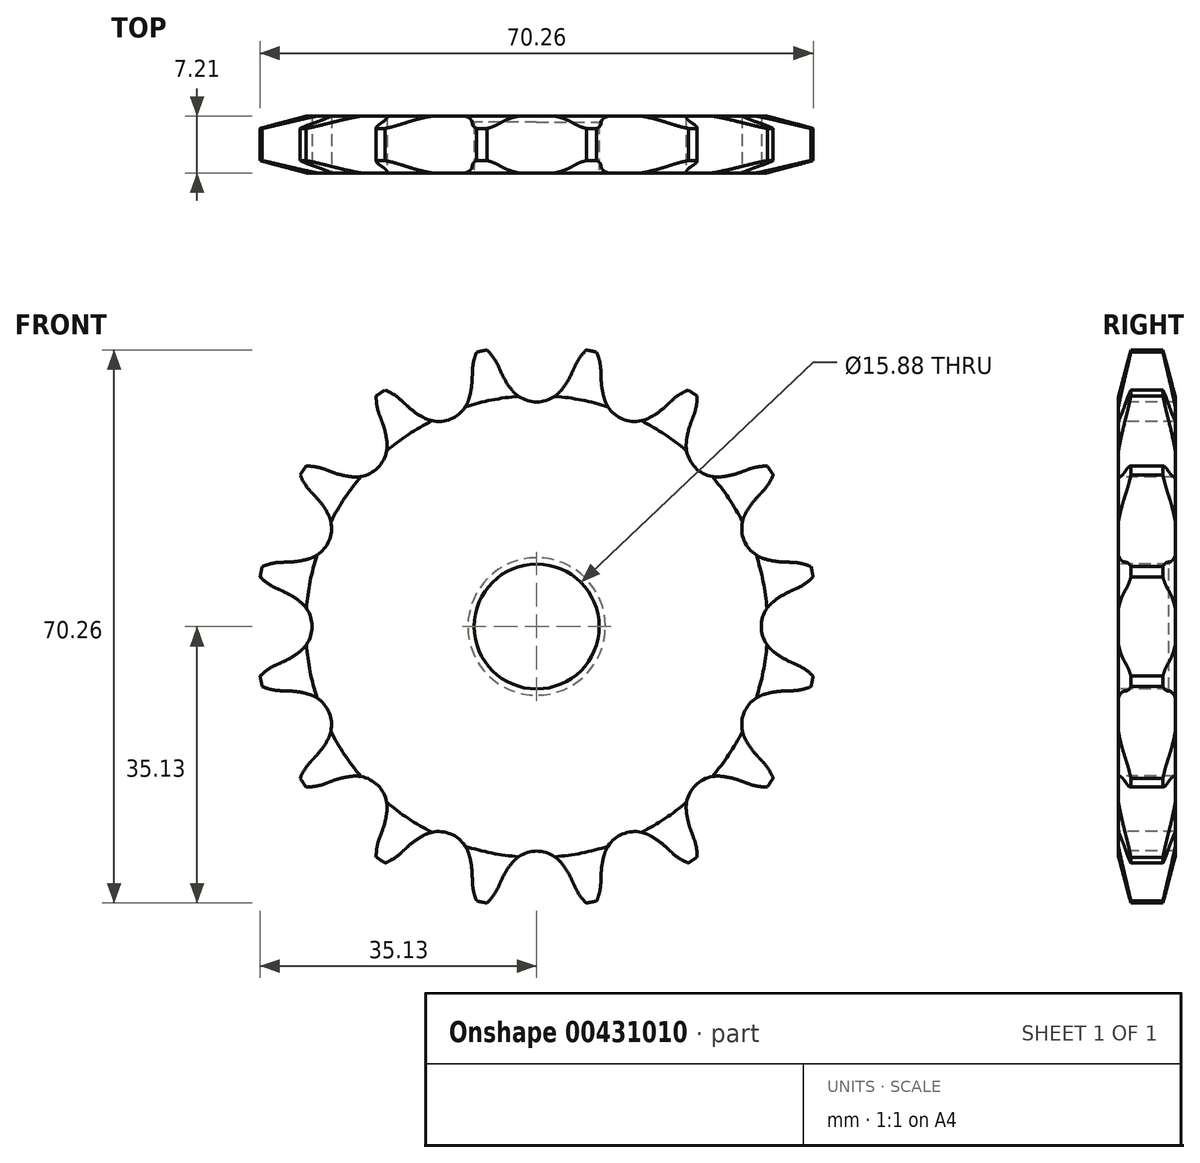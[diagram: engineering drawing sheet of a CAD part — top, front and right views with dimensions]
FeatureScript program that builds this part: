
annotation { "Feature Type Name" : "Feature", "Feature Type Description" : "" }
export const myFeature = defineFeature(function(context is Context, id is Id, definition is map)
    precondition{}
    {
        {
            var Q0;
            Q0=qCreatedBy(makeId("Right.planeOp"),FACE);
            var sketch = newSketch(context, id + "F0", { "sketchPlane" : qUnion([Q0])});
            skLineSegment(sketch, "E0", {"start": v(0, 0) * mm, "end": v(7.21, 0) * mm, "construction": true});
            skLineSegment(sketch, "E1", {"start": v(0, 35.69) * mm, "end": v(7.21, 35.69) * mm});
            skLineSegment(sketch, "E2", {"start": v(7.21, 35.69) * mm, "end": v(7.21, 25.4) * mm});
            skLineSegment(sketch, "E3", {"start": v(7.21, 25.4) * mm, "end": v(7.21, 25.4) * mm});
            skLineSegment(sketch, "E4", {"start": v(7.21, 25.4) * mm, "end": v(7.21, 7.94) * mm});
            skLineSegment(sketch, "E5", {"start": v(7.21, 7.94) * mm, "end": v(0, 7.94) * mm});
            skLineSegment(sketch, "E6", {"start": v(0, 7.94) * mm, "end": v(0, 35.69) * mm});
            skLineSegment(sketch, "E7.0.MirrorCS", {"start": v(0, -35.69) * mm, "end": v(7.21, -35.69) * mm});
            skLineSegment(sketch, "E7.1.MirrorCS", {"start": v(7.21, -35.69) * mm, "end": v(7.21, -25.4) * mm});
            skLineSegment(sketch, "E7.2.MirrorCS", {"start": v(7.21, -7.94) * mm, "end": v(0, -7.94) * mm});
            skLineSegment(sketch, "E7.3.MirrorCS", {"start": v(7.21, -25.4) * mm, "end": v(7.21, -7.94) * mm});
            skLineSegment(sketch, "E7.4.MirrorCS", {"start": v(7.21, -25.4) * mm, "end": v(7.21, -25.4) * mm});
            skLineSegment(sketch, "E7.5.MirrorCS", {"start": v(0, -7.94) * mm, "end": v(0, -35.69) * mm});
            skSolve(sketch);
        }
        {
            var Q0;
            Q0=makeQuery(id+"F0.imprint","IMPRINT",FACE,{"disambiguationData":[TD([[makeQuery(id+"F0.imprint","IMPRINT",EDGE,{"derivedFrom":sQuery(id+"F0.wireOp",EDGE,"E1")}),-1.0]])]});
            var Q1;
            Q1=sQuery(id+"F0.wireOp",EDGE,"E0");
            revolve(context, id + "F1", {"entities" : qUnion([Q0]), "axis" : qUnion([Q1]), "revolveType" : RevolveType.FULL});
        }
        {
            var Q0;
            Q0=makeQuery(id+"F1.opRevolve","SWEPT_EDGE",EDGE,{"disambiguationData":[OSD([sQuery(id+"F0.wireOp",EDGE,"E1"),sQuery(id+"F0.wireOp",EDGE,"E6")])]});
            var Q1;
            Q1=makeQuery(id+"F1.opRevolve","SWEPT_EDGE",EDGE,{"disambiguationData":[OSD([sQuery(id+"F0.wireOp",EDGE,"E1"),sQuery(id+"F0.wireOp",EDGE,"E2")])]});
            chamfer(context, id + "F2", {"entities" : qUnion([Q0, Q1]), "chamferType" : ChamferType.TWO_OFFSETS, "width1" : 6.35 * mm, "oppositeDirection" : false, "width2" : 1.57 * mm, "tangentPropagation" : true});
        }
        {
            var Q0;
            Q0=makeQuery(id+"F1.opRevolve","SWEPT_FACE",FACE,{"disambiguationData":[OSD([sQuery(id+"F0.wireOp",EDGE,"E6")])]});
            var sketch = newSketch(context, id + "F3", { "sketchPlane" : qUnion([Q0])});
            skCircle(sketch, "E8", {"center": v(0, 0) * mm, "radius": 32.55 * mm, "construction": true});
            skLineSegment(sketch, "E9", {"start": v(0, 0) * mm, "end": v(0, 32.55) * mm, "construction": true});
            skLineSegment(sketch, "E10", {"start": v(0, 32.55) * mm, "end": v(25.8, 32.55) * mm, "construction": true});
            skPoint(sketch, "E11", {"position": v(-10.88, 30.38) * mm});
            skPoint(sketch, "E12", {"position": v(4.95, 36.52) * mm});
            skLineSegment(sketch, "E13", {"start": v(0, 32.55) * mm, "end": v(4.95, 36.52) * mm, "construction": true});
            skLineSegment(sketch, "E14", {"start": v(4.95, 36.52) * mm, "end": v(-4.5, 32.26) * mm, "construction": true});
            skLineSegment(sketch, "E15", {"start": v(-4.5, 32.26) * mm, "end": v(-4.88, 33.1) * mm});
            skLineSegment(sketch, "E16", {"start": v(0, 0) * mm, "end": v(-7.12, 35.8) * mm, "construction": true});
            skArc(sketch, "E17", {"start": v(-7.12, 35.8) * mm, "mid": v(-15.95, 26.17) * mm, "end": v(-4.88, 33.1) * mm, "construction": true});
            skArc(sketch, "E18", {"start": v(-4.88, 33.1) * mm, "mid": v(-5.81, 34.6) * mm, "end": v(-7.12, 35.8) * mm});
            skArc(sketch, "E19", {"start": v(-3.14, 30.03) * mm, "mid": v(13.78, 41.93) * mm, "end": v(-4.5, 32.26) * mm, "construction": true});
            skArc(sketch, "E20", {"start": v(-4.5, 32.26) * mm, "mid": v(-3.89, 31.1) * mm, "end": v(-3.14, 30.03) * mm});
            skLineSegment(sketch, "E21", {"start": v(4.4, 12.5) * mm, "end": v(-4.88, 33.1) * mm, "construction": true});
            skArc(sketch, "E22.0.MirrorCS", {"start": v(4.5, 32.26) * mm, "mid": v(3.89, 31.1) * mm, "end": v(3.14, 30.03) * mm});
            skLineSegment(sketch, "E23.0.MirrorCS", {"start": v(4.5, 32.26) * mm, "end": v(4.88, 33.1) * mm});
            skArc(sketch, "E24.0.MirrorCS", {"start": v(4.88, 33.1) * mm, "mid": v(5.81, 34.6) * mm, "end": v(7.12, 35.8) * mm});
            skArc(sketch, "E25", {"start": v(-3.14, 30.03) * mm, "mid": v(0, 28.53) * mm, "end": v(3.14, 30.03) * mm});
            skArc(sketch, "E26", {"start": v(3.14, 30.03) * mm, "mid": v(0, 36.57) * mm, "end": v(-3.14, 30.03) * mm, "construction": true});
            skArc(sketch, "E27.1.0", {"start": v(-17.17, 28.7) * mm, "mid": v(-18.61, 29.74) * mm, "end": v(-20.28, 30.34) * mm});
            skLineSegment(sketch, "E27.1.1", {"start": v(-16.5, 28.08) * mm, "end": v(-17.17, 28.7) * mm});
            skArc(sketch, "E27.1.2", {"start": v(-16.5, 28.08) * mm, "mid": v(-15.5, 27.25) * mm, "end": v(-14.39, 26.55) * mm});
            skArc(sketch, "E27.1.3", {"start": v(-14.39, 26.55) * mm, "mid": v(-10.92, 26.36) * mm, "end": v(-8.6, 28.95) * mm});
            skArc(sketch, "E27.1.4", {"start": v(-8.19, 31.53) * mm, "mid": v(-8.3, 30.22) * mm, "end": v(-8.6, 28.95) * mm});
            skLineSegment(sketch, "E27.1.5", {"start": v(-8.19, 31.53) * mm, "end": v(-8.16, 32.44) * mm});
            skArc(sketch, "E27.1.6", {"start": v(-8.16, 32.44) * mm, "mid": v(-7.87, 34.19) * mm, "end": v(-7.12, 35.8) * mm});
            skArc(sketch, "E27.2.0", {"start": v(-26.85, 19.95) * mm, "mid": v(-28.57, 20.35) * mm, "end": v(-30.34, 20.28) * mm});
            skLineSegment(sketch, "E27.2.1", {"start": v(-26, 19.63) * mm, "end": v(-26.85, 19.95) * mm});
            skArc(sketch, "E27.2.2", {"start": v(-26, 19.63) * mm, "mid": v(-24.74, 19.24) * mm, "end": v(-23.45, 19.02) * mm});
            skArc(sketch, "E27.2.3", {"start": v(-23.45, 19.02) * mm, "mid": v(-20.17, 20.17) * mm, "end": v(-19.02, 23.45) * mm});
            skArc(sketch, "E27.2.4", {"start": v(-19.63, 26) * mm, "mid": v(-19.24, 24.74) * mm, "end": v(-19.02, 23.45) * mm});
            skLineSegment(sketch, "E27.2.5", {"start": v(-19.63, 26) * mm, "end": v(-19.95, 26.85) * mm});
            skArc(sketch, "E27.2.6", {"start": v(-19.95, 26.85) * mm, "mid": v(-20.35, 28.57) * mm, "end": v(-20.28, 30.34) * mm});
            skArc(sketch, "E27.3.0", {"start": v(-32.44, 8.16) * mm, "mid": v(-34.19, 7.87) * mm, "end": v(-35.8, 7.12) * mm});
            skLineSegment(sketch, "E27.3.1", {"start": v(-31.53, 8.19) * mm, "end": v(-32.44, 8.16) * mm});
            skArc(sketch, "E27.3.2", {"start": v(-31.53, 8.19) * mm, "mid": v(-30.22, 8.3) * mm, "end": v(-28.95, 8.6) * mm});
            skArc(sketch, "E27.3.3", {"start": v(-28.95, 8.6) * mm, "mid": v(-26.36, 10.92) * mm, "end": v(-26.55, 14.39) * mm});
            skArc(sketch, "E27.3.4", {"start": v(-28.08, 16.5) * mm, "mid": v(-27.25, 15.5) * mm, "end": v(-26.55, 14.39) * mm});
            skLineSegment(sketch, "E27.3.5", {"start": v(-28.08, 16.5) * mm, "end": v(-28.7, 17.17) * mm});
            skArc(sketch, "E27.3.6", {"start": v(-28.7, 17.17) * mm, "mid": v(-29.74, 18.61) * mm, "end": v(-30.34, 20.28) * mm});
            skArc(sketch, "E27.4.0", {"start": v(-33.1, -4.88) * mm, "mid": v(-34.6, -5.81) * mm, "end": v(-35.8, -7.12) * mm});
            skLineSegment(sketch, "E27.4.1", {"start": v(-32.26, -4.5) * mm, "end": v(-33.1, -4.88) * mm});
            skArc(sketch, "E27.4.2", {"start": v(-32.26, -4.5) * mm, "mid": v(-31.1, -3.89) * mm, "end": v(-30.03, -3.14) * mm});
            skArc(sketch, "E27.4.3", {"start": v(-30.03, -3.14) * mm, "mid": v(-28.53, 0) * mm, "end": v(-30.03, 3.14) * mm});
            skArc(sketch, "E27.4.4", {"start": v(-32.26, 4.5) * mm, "mid": v(-31.1, 3.89) * mm, "end": v(-30.03, 3.14) * mm});
            skLineSegment(sketch, "E27.4.5", {"start": v(-32.26, 4.5) * mm, "end": v(-33.1, 4.88) * mm});
            skArc(sketch, "E27.4.6", {"start": v(-33.1, 4.88) * mm, "mid": v(-34.6, 5.81) * mm, "end": v(-35.8, 7.12) * mm});
            skArc(sketch, "E27.5.0", {"start": v(-28.7, -17.17) * mm, "mid": v(-29.74, -18.61) * mm, "end": v(-30.34, -20.28) * mm});
            skLineSegment(sketch, "E27.5.1", {"start": v(-28.08, -16.5) * mm, "end": v(-28.7, -17.17) * mm});
            skArc(sketch, "E27.5.2", {"start": v(-28.08, -16.5) * mm, "mid": v(-27.25, -15.5) * mm, "end": v(-26.55, -14.39) * mm});
            skArc(sketch, "E27.5.3", {"start": v(-26.55, -14.39) * mm, "mid": v(-26.36, -10.92) * mm, "end": v(-28.95, -8.6) * mm});
            skArc(sketch, "E27.5.4", {"start": v(-31.53, -8.19) * mm, "mid": v(-30.22, -8.3) * mm, "end": v(-28.95, -8.6) * mm});
            skLineSegment(sketch, "E27.5.5", {"start": v(-31.53, -8.19) * mm, "end": v(-32.44, -8.16) * mm});
            skArc(sketch, "E27.5.6", {"start": v(-32.44, -8.16) * mm, "mid": v(-34.19, -7.87) * mm, "end": v(-35.8, -7.12) * mm});
            skArc(sketch, "E27.6.0", {"start": v(-19.95, -26.85) * mm, "mid": v(-20.35, -28.57) * mm, "end": v(-20.28, -30.34) * mm});
            skLineSegment(sketch, "E27.6.1", {"start": v(-19.63, -26) * mm, "end": v(-19.95, -26.85) * mm});
            skArc(sketch, "E27.6.2", {"start": v(-19.63, -26) * mm, "mid": v(-19.24, -24.74) * mm, "end": v(-19.02, -23.45) * mm});
            skArc(sketch, "E27.6.3", {"start": v(-19.02, -23.45) * mm, "mid": v(-20.17, -20.17) * mm, "end": v(-23.45, -19.02) * mm});
            skArc(sketch, "E27.6.4", {"start": v(-26, -19.63) * mm, "mid": v(-24.74, -19.24) * mm, "end": v(-23.45, -19.02) * mm});
            skLineSegment(sketch, "E27.6.5", {"start": v(-26, -19.63) * mm, "end": v(-26.85, -19.95) * mm});
            skArc(sketch, "E27.6.6", {"start": v(-26.85, -19.95) * mm, "mid": v(-28.57, -20.35) * mm, "end": v(-30.34, -20.28) * mm});
            skArc(sketch, "E27.7.0", {"start": v(-8.16, -32.44) * mm, "mid": v(-7.87, -34.19) * mm, "end": v(-7.12, -35.8) * mm});
            skLineSegment(sketch, "E27.7.1", {"start": v(-8.19, -31.53) * mm, "end": v(-8.16, -32.44) * mm});
            skArc(sketch, "E27.7.2", {"start": v(-8.19, -31.53) * mm, "mid": v(-8.3, -30.22) * mm, "end": v(-8.6, -28.95) * mm});
            skArc(sketch, "E27.7.3", {"start": v(-8.6, -28.95) * mm, "mid": v(-10.92, -26.36) * mm, "end": v(-14.39, -26.55) * mm});
            skArc(sketch, "E27.7.4", {"start": v(-16.5, -28.08) * mm, "mid": v(-15.5, -27.25) * mm, "end": v(-14.39, -26.55) * mm});
            skLineSegment(sketch, "E27.7.5", {"start": v(-16.5, -28.08) * mm, "end": v(-17.17, -28.7) * mm});
            skArc(sketch, "E27.7.6", {"start": v(-17.17, -28.7) * mm, "mid": v(-18.61, -29.74) * mm, "end": v(-20.28, -30.34) * mm});
            skArc(sketch, "E27.8.0", {"start": v(4.88, -33.1) * mm, "mid": v(5.81, -34.6) * mm, "end": v(7.12, -35.8) * mm});
            skLineSegment(sketch, "E27.8.1", {"start": v(4.5, -32.26) * mm, "end": v(4.88, -33.1) * mm});
            skArc(sketch, "E27.8.2", {"start": v(4.5, -32.26) * mm, "mid": v(3.89, -31.1) * mm, "end": v(3.14, -30.03) * mm});
            skArc(sketch, "E27.8.3", {"start": v(3.14, -30.03) * mm, "mid": v(0, -28.53) * mm, "end": v(-3.14, -30.03) * mm});
            skArc(sketch, "E27.8.4", {"start": v(-4.5, -32.26) * mm, "mid": v(-3.89, -31.1) * mm, "end": v(-3.14, -30.03) * mm});
            skLineSegment(sketch, "E27.8.5", {"start": v(-4.5, -32.26) * mm, "end": v(-4.88, -33.1) * mm});
            skArc(sketch, "E27.8.6", {"start": v(-4.88, -33.1) * mm, "mid": v(-5.81, -34.6) * mm, "end": v(-7.12, -35.8) * mm});
            skArc(sketch, "E27.9.0", {"start": v(17.17, -28.7) * mm, "mid": v(18.61, -29.74) * mm, "end": v(20.28, -30.34) * mm});
            skLineSegment(sketch, "E27.9.1", {"start": v(16.5, -28.08) * mm, "end": v(17.17, -28.7) * mm});
            skArc(sketch, "E27.9.2", {"start": v(16.5, -28.08) * mm, "mid": v(15.5, -27.25) * mm, "end": v(14.39, -26.55) * mm});
            skArc(sketch, "E27.9.3", {"start": v(14.39, -26.55) * mm, "mid": v(10.92, -26.36) * mm, "end": v(8.6, -28.95) * mm});
            skArc(sketch, "E27.9.4", {"start": v(8.19, -31.53) * mm, "mid": v(8.3, -30.22) * mm, "end": v(8.6, -28.95) * mm});
            skLineSegment(sketch, "E27.9.5", {"start": v(8.19, -31.53) * mm, "end": v(8.16, -32.44) * mm});
            skArc(sketch, "E27.9.6", {"start": v(8.16, -32.44) * mm, "mid": v(7.87, -34.19) * mm, "end": v(7.12, -35.8) * mm});
            skArc(sketch, "E27.10.0", {"start": v(26.85, -19.95) * mm, "mid": v(28.57, -20.35) * mm, "end": v(30.34, -20.28) * mm});
            skLineSegment(sketch, "E27.10.1", {"start": v(26, -19.63) * mm, "end": v(26.85, -19.95) * mm});
            skArc(sketch, "E27.10.2", {"start": v(26, -19.63) * mm, "mid": v(24.74, -19.24) * mm, "end": v(23.45, -19.02) * mm});
            skArc(sketch, "E27.10.3", {"start": v(23.45, -19.02) * mm, "mid": v(20.17, -20.17) * mm, "end": v(19.02, -23.45) * mm});
            skArc(sketch, "E27.10.4", {"start": v(19.63, -26) * mm, "mid": v(19.24, -24.74) * mm, "end": v(19.02, -23.45) * mm});
            skLineSegment(sketch, "E27.10.5", {"start": v(19.63, -26) * mm, "end": v(19.95, -26.85) * mm});
            skArc(sketch, "E27.10.6", {"start": v(19.95, -26.85) * mm, "mid": v(20.35, -28.57) * mm, "end": v(20.28, -30.34) * mm});
            skArc(sketch, "E27.11.0", {"start": v(32.44, -8.16) * mm, "mid": v(34.19, -7.87) * mm, "end": v(35.8, -7.12) * mm});
            skLineSegment(sketch, "E27.11.1", {"start": v(31.53, -8.19) * mm, "end": v(32.44, -8.16) * mm});
            skArc(sketch, "E27.11.2", {"start": v(31.53, -8.19) * mm, "mid": v(30.22, -8.3) * mm, "end": v(28.95, -8.6) * mm});
            skArc(sketch, "E27.11.3", {"start": v(28.95, -8.6) * mm, "mid": v(26.36, -10.92) * mm, "end": v(26.55, -14.39) * mm});
            skArc(sketch, "E27.11.4", {"start": v(28.08, -16.5) * mm, "mid": v(27.25, -15.5) * mm, "end": v(26.55, -14.39) * mm});
            skLineSegment(sketch, "E27.11.5", {"start": v(28.08, -16.5) * mm, "end": v(28.7, -17.17) * mm});
            skArc(sketch, "E27.11.6", {"start": v(28.7, -17.17) * mm, "mid": v(29.74, -18.61) * mm, "end": v(30.34, -20.28) * mm});
            skArc(sketch, "E27.12.0", {"start": v(33.1, 4.88) * mm, "mid": v(34.6, 5.81) * mm, "end": v(35.8, 7.12) * mm});
            skLineSegment(sketch, "E27.12.1", {"start": v(32.26, 4.5) * mm, "end": v(33.1, 4.88) * mm});
            skArc(sketch, "E27.12.2", {"start": v(32.26, 4.5) * mm, "mid": v(31.1, 3.89) * mm, "end": v(30.03, 3.14) * mm});
            skArc(sketch, "E27.12.3", {"start": v(30.03, 3.14) * mm, "mid": v(28.53, 0) * mm, "end": v(30.03, -3.14) * mm});
            skArc(sketch, "E27.12.4", {"start": v(32.26, -4.5) * mm, "mid": v(31.1, -3.89) * mm, "end": v(30.03, -3.14) * mm});
            skLineSegment(sketch, "E27.12.5", {"start": v(32.26, -4.5) * mm, "end": v(33.1, -4.88) * mm});
            skArc(sketch, "E27.12.6", {"start": v(33.1, -4.88) * mm, "mid": v(34.6, -5.81) * mm, "end": v(35.8, -7.12) * mm});
            skArc(sketch, "E27.13.0", {"start": v(28.7, 17.17) * mm, "mid": v(29.74, 18.61) * mm, "end": v(30.34, 20.28) * mm});
            skLineSegment(sketch, "E27.13.1", {"start": v(28.08, 16.5) * mm, "end": v(28.7, 17.17) * mm});
            skArc(sketch, "E27.13.2", {"start": v(28.08, 16.5) * mm, "mid": v(27.25, 15.5) * mm, "end": v(26.55, 14.39) * mm});
            skArc(sketch, "E27.13.3", {"start": v(26.55, 14.39) * mm, "mid": v(26.36, 10.92) * mm, "end": v(28.95, 8.6) * mm});
            skArc(sketch, "E27.13.4", {"start": v(31.53, 8.19) * mm, "mid": v(30.22, 8.3) * mm, "end": v(28.95, 8.6) * mm});
            skLineSegment(sketch, "E27.13.5", {"start": v(31.53, 8.19) * mm, "end": v(32.44, 8.16) * mm});
            skArc(sketch, "E27.13.6", {"start": v(32.44, 8.16) * mm, "mid": v(34.19, 7.87) * mm, "end": v(35.8, 7.12) * mm});
            skArc(sketch, "E27.14.0", {"start": v(19.95, 26.85) * mm, "mid": v(20.35, 28.57) * mm, "end": v(20.28, 30.34) * mm});
            skLineSegment(sketch, "E27.14.1", {"start": v(19.63, 26) * mm, "end": v(19.95, 26.85) * mm});
            skArc(sketch, "E27.14.2", {"start": v(19.63, 26) * mm, "mid": v(19.24, 24.74) * mm, "end": v(19.02, 23.45) * mm});
            skArc(sketch, "E27.14.3", {"start": v(19.02, 23.45) * mm, "mid": v(20.17, 20.17) * mm, "end": v(23.45, 19.02) * mm});
            skArc(sketch, "E27.14.4", {"start": v(26, 19.63) * mm, "mid": v(24.74, 19.24) * mm, "end": v(23.45, 19.02) * mm});
            skLineSegment(sketch, "E27.14.5", {"start": v(26, 19.63) * mm, "end": v(26.85, 19.95) * mm});
            skArc(sketch, "E27.14.6", {"start": v(26.85, 19.95) * mm, "mid": v(28.57, 20.35) * mm, "end": v(30.34, 20.28) * mm});
            skArc(sketch, "E27.15.0", {"start": v(8.16, 32.44) * mm, "mid": v(7.87, 34.19) * mm, "end": v(7.12, 35.8) * mm});
            skLineSegment(sketch, "E27.15.1", {"start": v(8.19, 31.53) * mm, "end": v(8.16, 32.44) * mm});
            skArc(sketch, "E27.15.2", {"start": v(8.19, 31.53) * mm, "mid": v(8.3, 30.22) * mm, "end": v(8.6, 28.95) * mm});
            skArc(sketch, "E27.15.3", {"start": v(8.6, 28.95) * mm, "mid": v(10.92, 26.36) * mm, "end": v(14.39, 26.55) * mm});
            skArc(sketch, "E27.15.4", {"start": v(16.5, 28.08) * mm, "mid": v(15.5, 27.25) * mm, "end": v(14.39, 26.55) * mm});
            skLineSegment(sketch, "E27.15.5", {"start": v(16.5, 28.08) * mm, "end": v(17.17, 28.7) * mm});
            skArc(sketch, "E27.15.6", {"start": v(17.17, 28.7) * mm, "mid": v(18.61, 29.74) * mm, "end": v(20.28, 30.34) * mm});
            skSolve(sketch);
        }
        {
            var Q0;
            Q0=qSketchRegion(id+"F3",true);
            extrude(context, id + "F4", {"entities" : qUnion([Q0]), "operationType" : NewBodyOperationType.INTERSECT, "endBound" : BoundingType.THROUGH_ALL, "oppositeDirection" : true, "depth" : 25.4 * mm});
        }
        {
            var Q0;
            Q0=makeQuery(id+"F1.opRevolve","SWEPT_EDGE",EDGE,{"disambiguationData":[OSD([sQuery(id+"F0.wireOp",EDGE,"E3"),sQuery(id+"F0.wireOp",EDGE,"E4")])]});
            chamfer(context, id + "F5", {"entities" : qUnion([Q0]), "width" : 0.8 * mm, "tangentPropagation" : true});
        }
    });
